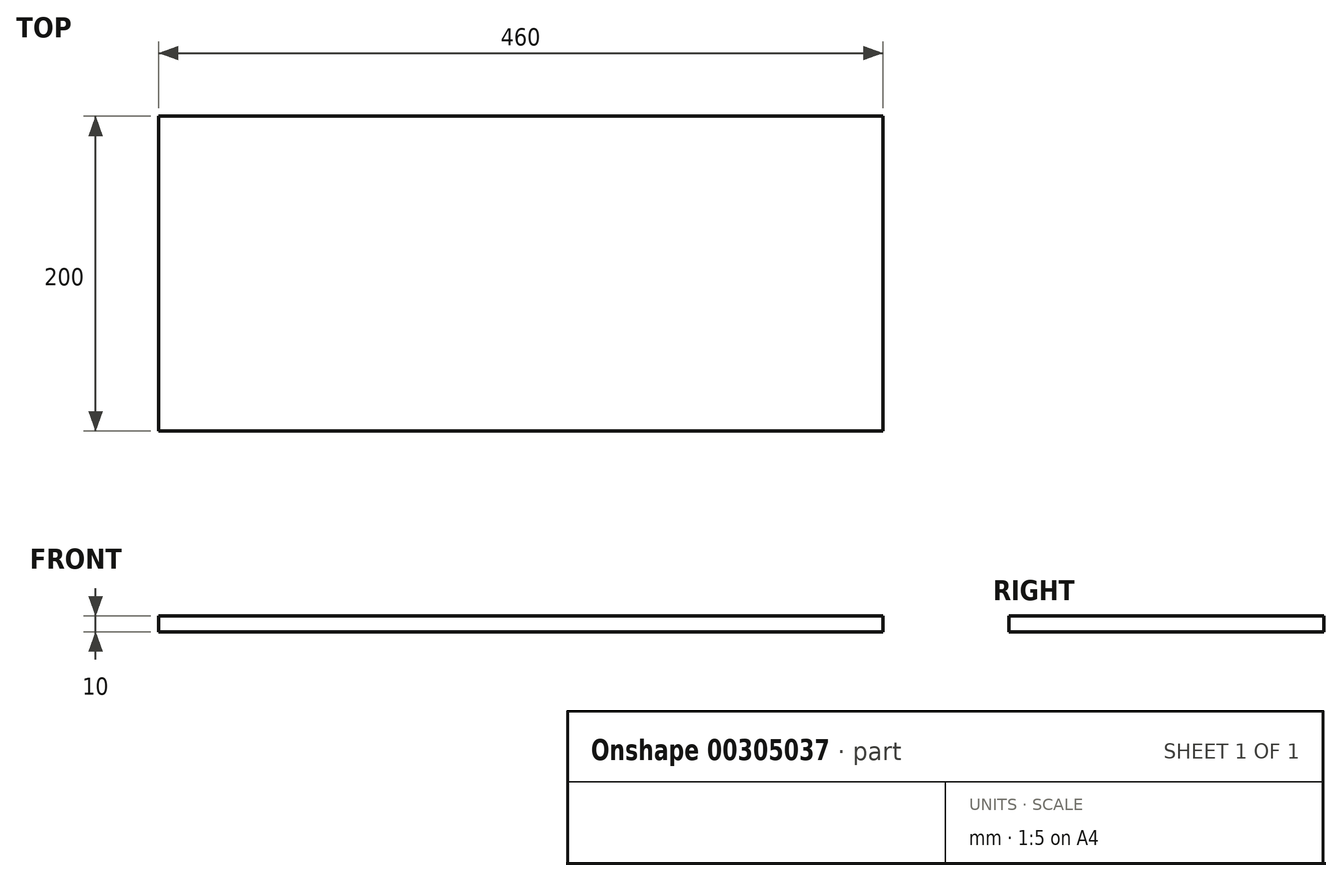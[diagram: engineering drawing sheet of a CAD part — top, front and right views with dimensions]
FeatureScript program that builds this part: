
annotation { "Feature Type Name" : "Feature", "Feature Type Description" : "" }
export const myFeature = defineFeature(function(context is Context, id is Id, definition is map)
    precondition{}
    {
        {
            var Q0;
            Q0=qCreatedBy(makeId("Top.planeOp"),FACE);
            var sketch = newSketch(context, id + "F0", { "sketchPlane" : qUnion([Q0])});
            skLineSegment(sketch, "E0.bottom", {"start": v(0, 0) * mm, "end": v(460, 0) * mm});
            skLineSegment(sketch, "E0.top", {"start": v(0, 200) * mm, "end": v(460, 200) * mm});
            skLineSegment(sketch, "E0.left", {"start": v(0, 0) * mm, "end": v(0, 200) * mm});
            skLineSegment(sketch, "E0.right", {"start": v(460, 0) * mm, "end": v(460, 200) * mm});
            skSolve(sketch);
        }
        {
            var Q0;
            Q0 = qSketchRegion(id + "F0", true);
            extrude(context, id + "F1", {"entities" : qUnion([Q0]), "depth" : 10 * mm});
        }
    });
